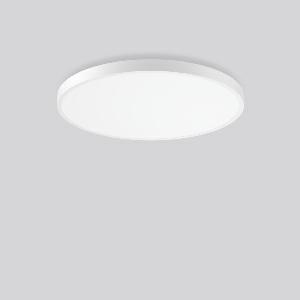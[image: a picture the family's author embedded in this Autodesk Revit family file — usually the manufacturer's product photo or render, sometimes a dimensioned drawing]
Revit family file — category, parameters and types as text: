
# Revit family: triona_round_a_312388_002_1_730_ad4b
name_source: partatom
category: Lighting Fixtures
units: mm (PartAtom-declared; Revit-internal decimal feet)

## family parameters
Cut with Voids When Loaded = No
Host = Face
Light Source = No
Part Type = Normal
Room Calculation Point = No
Round Connector Dimension = Use Diameter
Shared = No

## types (1)
- TRIONA round A (1 x LED Modul 840, 12900 lm, 4000)
    Apparent Load = 133 VA
    CIE Flux Codes = 49 80 96 71 100
    Color Rendering = 80
    Color Temperature = 4000
    Default Elevation = 1800 mm
    Description = Series: TRIONA round
Decorative round LED surface-mounted luminaire. Flat, seamless frame: aluminium extrusion profile, powder coated. Cover made of sheet steel, powder-coated. Direct light emission through a diffuser plastic opal. Indirect light emission through a flush diffuser made of satin-finish plastic. Lightguide and diffuser made of non-yellowing plastic (PMMA). Lateral light emission (RZB SIDELITE technology) for above-average homogeneous light distribution. Direct 70%, indirect 30% light emission. Suitable for Ceiling mounting, Wall (surface). Tool-free mounting via bayonet connection. Electronic ballast included. Very easy installation thanks to Plug+Play connection. With Casambi smart+free Bluetooth control for wireless network and operation using Android / iOS devices, free app available for download. 
Colour: traffic white, matt (RAL 9016)
Diameter: 845 mm
Height: 88 mm
Lamp: LED
Socket: without socket
Colour temperature: 4000K
Colour rendering index (CRI): 80
System power: 133 W
Rated luminous flux: 12900 lm
Luminous efficiency: 97 lm/W
Control gear: Dimmable Bluetooth converter
Protection class: I
Type of protection: IP 20
    Height = 88 mm
    Lamp = 1 x LED Modul 840
    Lamp Light Flux = 12900 lm
    Lamp count = 1
    Length = 845 mm
    Lifetime = 50000 h
    Luminous efficacy = 97 lm/W
    Manufacturer = RZB
    ModVariant = No
    Model = 312388.002.1.730
    Mounting Place = Ceiling
    Mounting Type = Surface mounted
    Number of Poles = 1
    OnlyDefault = Yes
    Power Factor = 1
    Product Name = TRIONA round A
    Product group = Surface mounted modular luminaires
    ProductGroupID = 306
    Protection Class = Protection class I
    Protection Degree = IP 20
    RLX_Detail_Level = 1
    RLX_Emergency_Light_Flux = 0 lm
    RLX_Emergency_Type = 0
    RLX_Emergency_Type_DB = No
    RlxData = <blob elided: 40317 chars, md5=8ab4dafb>
    Socket = socket
    Standby Power = 0 W
    System Light Flux = 12900 lm
    System Power = 133 W
    Type Comments = Product without accessories
    Type Image = 312388.002.jpg
    URL = http://relux.com
    VarID = ---
    Voltage = 230 V
    Voltage Range = 220-240 V
    Weight = 0.00 kg
    Width = 0 mm  [stored 0 ft]

note: [stored X ft] marks values corroborated as IEEE doubles in the binary element streams (Revit-internal decimal feet)

## geometry (parser evidence)
native form markers: Blend x4, Sweep x13
no freeform markers — native parametric forms only
